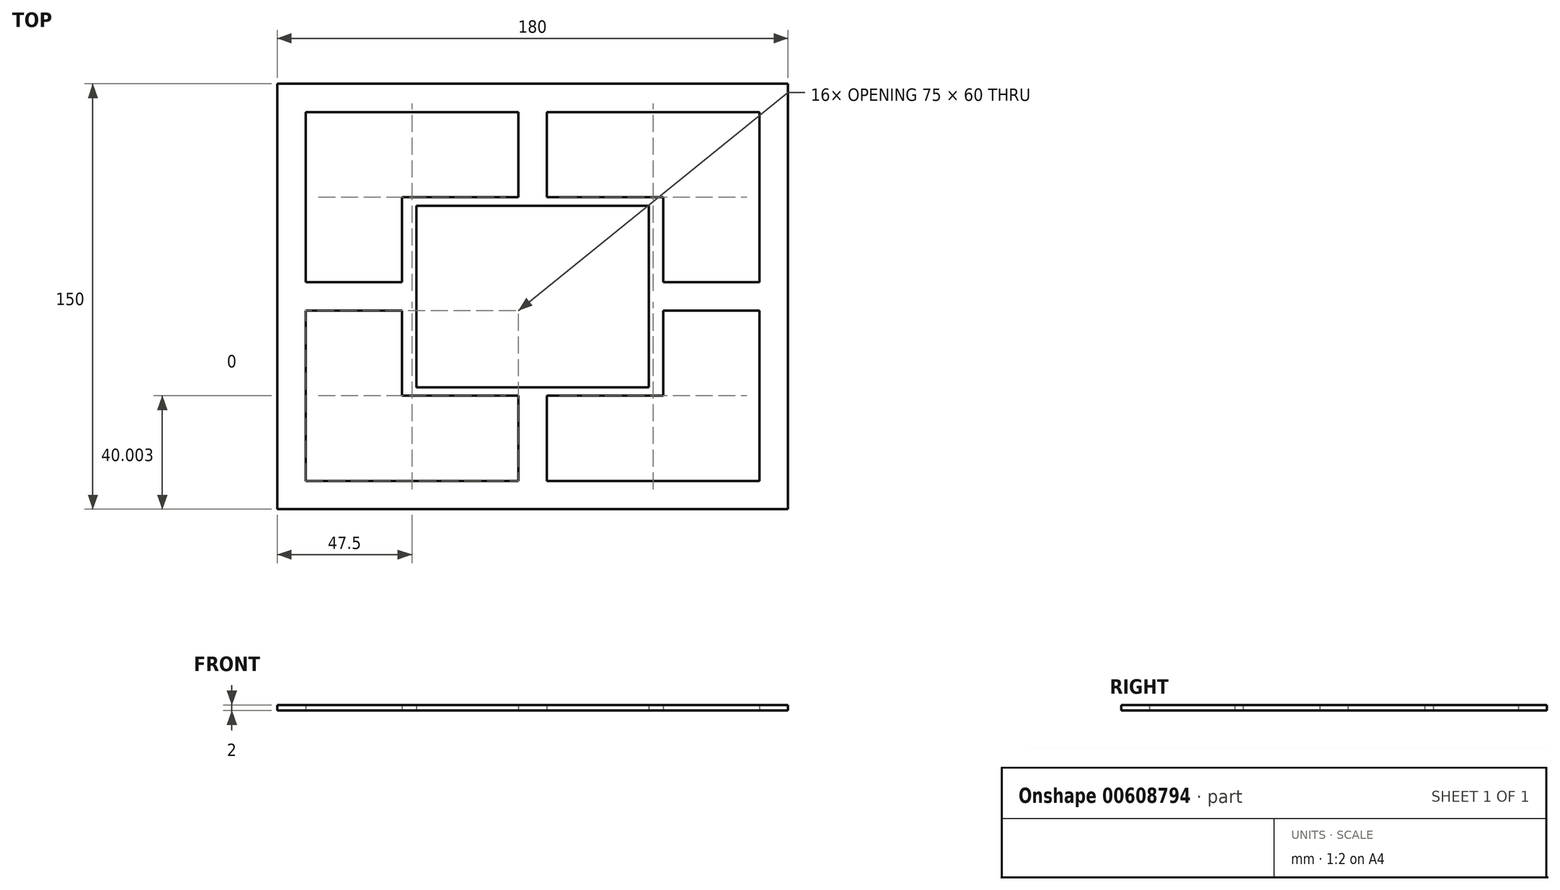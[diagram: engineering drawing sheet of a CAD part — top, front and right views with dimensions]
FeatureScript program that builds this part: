
annotation { "Feature Type Name" : "Feature", "Feature Type Description" : "" }
export const myFeature = defineFeature(function(context is Context, id is Id, definition is map)
    precondition{}
    {
        {
            var Q0;
            Q0=qCreatedBy(makeId("Top.planeOp"),FACE);
            var sketch = newSketch(context, id + "F0", { "sketchPlane" : qUnion([Q0])});
            skLineSegment(sketch, "E0.bottom", {"start": v(-88.74, 70.98) * mm, "end": v(91.26, 70.98) * mm});
            skLineSegment(sketch, "E0.top", {"start": v(-88.74, -79.02) * mm, "end": v(91.26, -79.02) * mm});
            skLineSegment(sketch, "E0.left", {"start": v(-88.74, 70.98) * mm, "end": v(-88.74, -79.02) * mm});
            skLineSegment(sketch, "E0.right", {"start": v(91.26, 70.98) * mm, "end": v(91.26, -79.02) * mm});
            skLineSegment(sketch, "E1", {"start": v(-88.74, 70.98) * mm, "end": v(-3.74, 70.98) * mm, "construction": true});
            skLineSegment(sketch, "E2", {"start": v(91.26, 70.98) * mm, "end": v(6.26, 70.98) * mm, "construction": true});
            skLineSegment(sketch, "E3", {"start": v(-88.74, 70.98) * mm, "end": v(-88.74, 0.98) * mm, "construction": true});
            skLineSegment(sketch, "E4", {"start": v(-88.74, -79.02) * mm, "end": v(-88.74, -9.02) * mm, "construction": true});
            skLineSegment(sketch, "E5.bottom", {"start": v(-3.74, 70.98) * mm, "end": v(6.26, 70.98) * mm});
            skLineSegment(sketch, "E5.top", {"start": v(-3.74, 70.98) * mm, "end": v(6.26, 70.98) * mm});
            skLineSegment(sketch, "E5.left", {"start": v(-3.74, 70.98) * mm, "end": v(-3.74, 70.98) * mm});
            skLineSegment(sketch, "E5.right", {"start": v(6.26, 70.98) * mm, "end": v(6.26, 70.98) * mm});
            skLineSegment(sketch, "E6.top", {"start": v(-3.74, -79.02) * mm, "end": v(6.26, -79.02) * mm});
            skLineSegment(sketch, "E6.left", {"start": v(-3.74, 60.98) * mm, "end": v(-3.74, 30.98) * mm});
            skLineSegment(sketch, "E6.right", {"start": v(6.26, 60.98) * mm, "end": v(6.26, 30.98) * mm});
            skLineSegment(sketch, "E7.bottom", {"start": v(-78.74, 0.98) * mm, "end": v(-44.74, 0.98) * mm});
            skLineSegment(sketch, "E7.top", {"start": v(-78.74, -9.02) * mm, "end": v(-44.74, -9.02) * mm});
            skLineSegment(sketch, "E7.left", {"start": v(-88.74, 0.98) * mm, "end": v(-88.74, -9.02) * mm});
            skLineSegment(sketch, "E7.right", {"start": v(91.26, 0.98) * mm, "end": v(91.26, -9.02) * mm});
            skLineSegment(sketch, "E8", {"start": v(-88.74, -4.02) * mm, "end": v(91.26, -4.02) * mm, "construction": true});
            skLineSegment(sketch, "E9", {"start": v(1.26, 70.98) * mm, "end": v(1.26, -4.02) * mm, "construction": true});
            skLineSegment(sketch, "E10.bottom", {"start": v(47.26, -39.02) * mm, "end": v(6.26, -39.02) * mm});
            skLineSegment(sketch, "E10.top", {"start": v(47.26, 30.98) * mm, "end": v(6.26, 30.98) * mm});
            skLineSegment(sketch, "E10.left", {"start": v(47.26, -39.02) * mm, "end": v(47.26, -9.02) * mm});
            skLineSegment(sketch, "E10.right", {"start": v(-44.74, -39.02) * mm, "end": v(-44.74, -9.02) * mm});
            skPoint(sketch, "E10.middle", {"position": v(1.26, -4.02) * mm});
            skLineSegment(sketch, "E11.trimOffspring", {"start": v(6.26, -39.02) * mm, "end": v(6.26, -69.02) * mm});
            skLineSegment(sketch, "E12.trimOffspring", {"start": v(47.26, 0.98) * mm, "end": v(81.26, 0.98) * mm});
            skLineSegment(sketch, "E13.trimOffspring", {"start": v(-3.74, -39.02) * mm, "end": v(-3.74, -69.02) * mm});
            skLineSegment(sketch, "E14.trimOffspring", {"start": v(47.26, -9.02) * mm, "end": v(81.26, -9.02) * mm});
            skLineSegment(sketch, "E15.trimOffspring", {"start": v(1.26, -9.02) * mm, "end": v(1.26, -79.02) * mm, "construction": true});
            skLineSegment(sketch, "E16.trimOffspring", {"start": v(47.26, 0.98) * mm, "end": v(47.26, 30.98) * mm});
            skLineSegment(sketch, "E17.trimOffspring", {"start": v(-3.74, 30.98) * mm, "end": v(-44.74, 30.98) * mm});
            skLineSegment(sketch, "E18.trimOffspring", {"start": v(-44.74, 0.98) * mm, "end": v(-44.74, 30.98) * mm});
            skLineSegment(sketch, "E19.trimOffspring", {"start": v(-3.74, -39.02) * mm, "end": v(-44.74, -39.02) * mm});
            skLineSegment(sketch, "E20.bottom", {"start": v(81.26, -69.02) * mm, "end": v(6.26, -69.02) * mm});
            skLineSegment(sketch, "E20.top", {"start": v(81.26, 60.98) * mm, "end": v(6.26, 60.98) * mm});
            skLineSegment(sketch, "E20.left", {"start": v(81.26, -69.02) * mm, "end": v(81.26, -9.02) * mm});
            skLineSegment(sketch, "E20.right", {"start": v(-78.74, -69.02) * mm, "end": v(-78.74, -9.02) * mm});
            skLineSegment(sketch, "E21.trimOffspring", {"start": v(-3.74, 60.98) * mm, "end": v(-78.74, 60.98) * mm});
            skLineSegment(sketch, "E22.trimOffspring", {"start": v(-78.74, 0.98) * mm, "end": v(-78.74, 60.98) * mm});
            skLineSegment(sketch, "E23.trimOffspring", {"start": v(-3.74, -69.02) * mm, "end": v(-78.74, -69.02) * mm});
            skLineSegment(sketch, "E24.trimOffspring", {"start": v(81.26, 0.98) * mm, "end": v(81.26, 60.98) * mm});
            skLineSegment(sketch, "E25.bottom", {"start": v(42.26, -36.02) * mm, "end": v(-39.74, -36.02) * mm});
            skLineSegment(sketch, "E25.top", {"start": v(42.26, 27.98) * mm, "end": v(-39.74, 27.98) * mm});
            skLineSegment(sketch, "E25.left", {"start": v(42.26, -36.02) * mm, "end": v(42.26, 27.98) * mm});
            skLineSegment(sketch, "E25.right", {"start": v(-39.74, -36.02) * mm, "end": v(-39.74, 27.98) * mm});
            skSolve(sketch);
        }
        {
            var Q0;
            Q0 = qSketchRegion(id + "F0", true);
            extrude(context, id + "F1", {"entities" : qUnion([Q0]), "depth" : 2 * mm, "offsetDistance" : 25 * mm});
        }
    });
